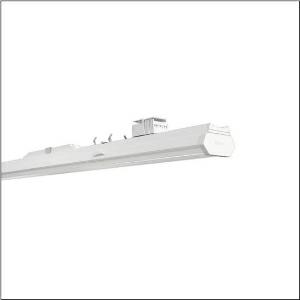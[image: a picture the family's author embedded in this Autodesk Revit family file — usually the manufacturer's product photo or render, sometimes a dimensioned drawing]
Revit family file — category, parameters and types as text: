
# Revit family: licross_r__21_protected_mo_52td11dn48xg_0db0
name_source: partatom
category: Lighting Fixtures
units: mm (PartAtom-declared; Revit-internal decimal feet)

## family parameters
Cut with Voids When Loaded = No
Host = Face
Light Source = No
Part Type = Normal
Room Calculation Point = No
Round Connector Dimension = Use Diameter
Shared = No

## types (1)
- --- (1 x LED, 8000 lm, 45.5 W, 4000K)
    Apparent Load = 46 VA
    CIE Flux Codes = 83 94 98 100 100
    Color Rendering = 80
    Color Temperature = 4000K
    Default Elevation = 1800 mm
    Description = Licross® 21 Protected MO, luminaire insert, of sheet steel, galvanised, coil coated, white, length: 1.500mm, width: 90mm, height: 103mm, LED rated luminous flux: 8.000lm, light colour: 840, control gear: DALI 2, with plug, 5-pole, with phase selection, mains connection: 220..240V, AC, 50/60Hz, rated input power: 46W, internal wiring halogen-free, primary light control with lens, of plastic, primary optical cover: cover, of PMMA, light emission: direct distribution, primary light characteristic: symmetric, protection rating (complete): IP54, insulation class (complete): insulation class I (protective earthing), certification: CE, ENEC, VDE, UKCA, protection symbol: D if used in an environment with non-conductive dust loads with corresponding accessories, impact resistance: IK06, permissible ambient temperature for indoor applications: -25..+45°C, corresponds to IFS (International Featured Standards) requirements for safety and quality in the food industry, reducing of maximum allowable ambient temperature of 5°C with ceiling mounting, LABS conformity tested according to VDMA 24364:2018-05, packaging unit: 1 piece
    Height = 92 mm
    Lamp = 1 x LED
    Lamp Light Flux = 8000 lm
    Lamp Power = 45.5 W
    Lamp count = 1
    Length = 1500 mm
    Luminous efficacy = 176 lm/W
    Manufacturer = Siteco
    ModVariant = No
    Model = 52TD11DN48XG
    Mounting Place = Ceiling
    Mounting Type = Pendant
    Number of Poles = 1
    OnlyDefault = Yes
    Power Factor = 1
    Product Name = Licross® 21 Protected MO
    Product group = luminaire insert | ceiling pendant
    ProductGroupID = 902
    Protection Class = Protection class I
    Protection Degree = IP 54
    RLX_Detail_Level = 1
    RLX_Emergency_Light_Flux = 0 lm
    RLX_Emergency_Type = 0
    RLX_Emergency_Type_DB = No
    RlxData = <blob elided: 24109 chars, md5=26a838f9>
    Socket = socket
    Standby Power = 0 W
    System Light Flux = 8000 lm
    System Power = 46 W
    Type Comments = factory setting: luminous flux: 100 % | dim-lin: 254 | 307 mA
    Type Image = l_1256148.jpg
    URL = http://relux.com
    VarID = @adj_149779
    Voltage = 0 V
    Weight = 0.00 kg
    Width = 88 mm

## geometry (parser evidence)
native form markers: Blend x4, Sweep x11
no freeform markers — native parametric forms only
